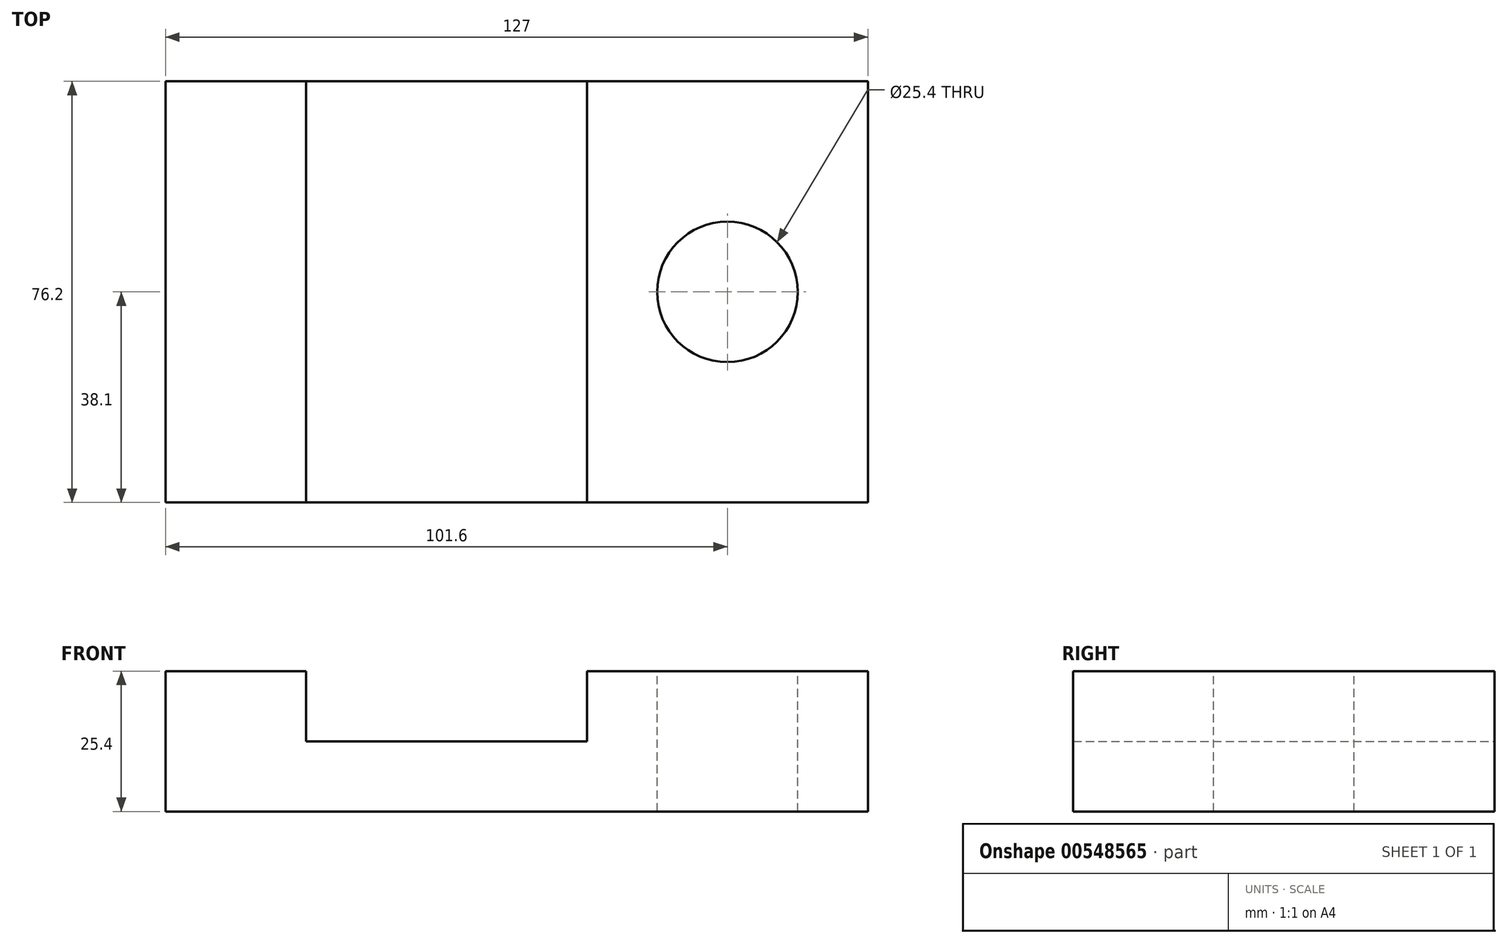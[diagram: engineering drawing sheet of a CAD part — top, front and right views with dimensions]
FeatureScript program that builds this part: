
annotation { "Feature Type Name" : "Feature", "Feature Type Description" : "" }
export const myFeature = defineFeature(function(context is Context, id is Id, definition is map)
    precondition{}
    {
        {
            var Q0;
            Q0=qCreatedBy(makeId("Front.planeOp"),FACE);
            var sketch = newSketch(context, id + "F0", { "sketchPlane" : qUnion([Q0])});
            skLineSegment(sketch, "E0", {"start": v(-45, -42.56) * mm, "end": v(82, -42.56) * mm});
            skLineSegment(sketch, "E1", {"start": v(82, -42.56) * mm, "end": v(82, -17.16) * mm});
            skLineSegment(sketch, "E2", {"start": v(82, -17.16) * mm, "end": v(31.2, -17.16) * mm});
            skLineSegment(sketch, "E3", {"start": v(31.2, -17.16) * mm, "end": v(31.2, -29.86) * mm});
            skLineSegment(sketch, "E4", {"start": v(31.2, -29.86) * mm, "end": v(-19.6, -29.86) * mm});
            skLineSegment(sketch, "E5", {"start": v(-19.6, -29.86) * mm, "end": v(-19.6, -17.16) * mm});
            skLineSegment(sketch, "E6", {"start": v(-19.6, -17.16) * mm, "end": v(-45, -17.16) * mm});
            skLineSegment(sketch, "E7", {"start": v(-45, -17.16) * mm, "end": v(-45, -42.56) * mm});
            skSolve(sketch);
        }
        {
            var Q0;
            Q0 = qSketchRegion(id + "F0", true);
            extrude(context, id + "F1", {"entities" : qUnion([Q0]), "depth" : 76.2 * mm, "offsetDistance" : 25.4 * mm});
        }
        {
            var Q0;
            Q0=makeQuery(id+"F1.opExtrude","SWEPT_FACE",FACE,{"disambiguationData":[OSD([sQuery(id+"F0.wireOp",EDGE,"E2")])]});
            var sketch = newSketch(context, id + "F2", { "sketchPlane" : qUnion([Q0])});
            skCircle(sketch, "E8", {"center": v(56.6, -38.1) * mm, "radius": 12.7 * mm});
            skSolve(sketch);
        }
        {
            var Q0;
            Q0=makeQuery(id+"F2.imprint","IMPRINT",FACE,{"disambiguationData":[TD([[makeQuery(id+"F2.imprint","IMPRINT",EDGE,{"derivedFrom":sQuery(id+"F2.wireOp",EDGE,"E8")}),1.0]])]});
            extrude(context, id + "F3", {"entities" : qUnion([Q0]), "operationType" : NewBodyOperationType.REMOVE, "oppositeDirection" : true, "depth" : 25.4 * mm, "offsetDistance" : 25.4 * mm});
        }
    });
